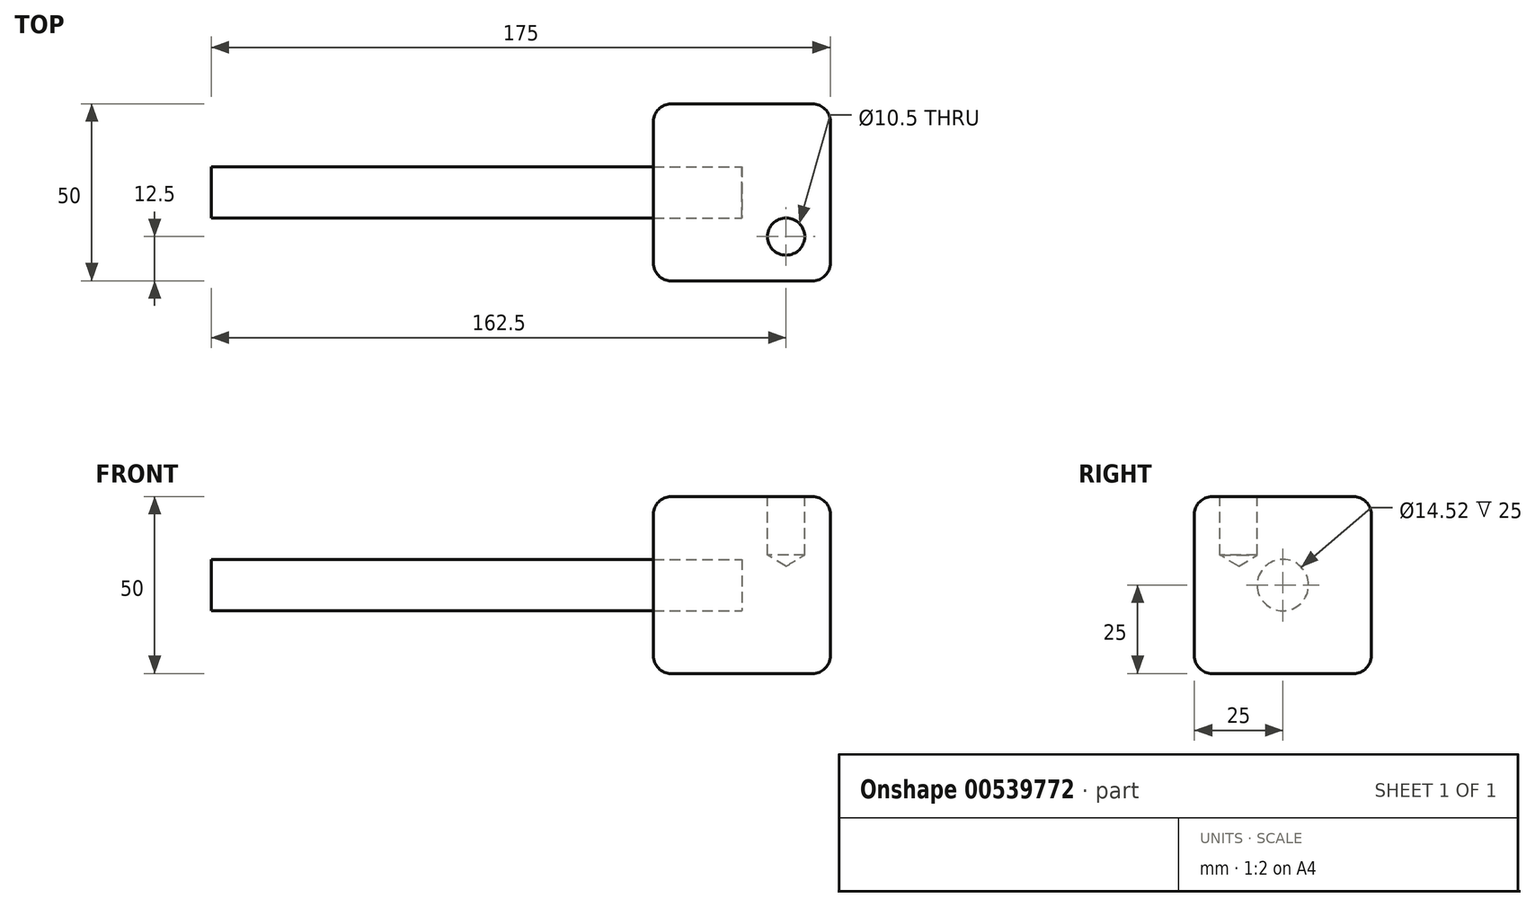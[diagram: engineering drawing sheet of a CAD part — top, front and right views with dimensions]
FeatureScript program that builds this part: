
annotation { "Feature Type Name" : "Feature", "Feature Type Description" : "" }
export const myFeature = defineFeature(function(context is Context, id is Id, definition is map)
    precondition{}
    {
        {
            var Q0;
            Q0=qCreatedBy(makeId("Front.planeOp"),FACE);
            var sketch = newSketch(context, id + "F0", { "sketchPlane" : qUnion([Q0])});
            skLineSegment(sketch, "E0.bottom", {"start": v(-25, 25) * mm, "end": v(25, 25) * mm});
            skLineSegment(sketch, "E0.top", {"start": v(-25, -25) * mm, "end": v(25, -25) * mm});
            skLineSegment(sketch, "E0.left", {"start": v(-25, 25) * mm, "end": v(-25, -25) * mm});
            skLineSegment(sketch, "E0.right", {"start": v(25, 25) * mm, "end": v(25, -25) * mm});
            skSolve(sketch);
        }
        {
            var Q0;
            Q0=makeQuery(id+"F0.imprint","IMPRINT",FACE,{"disambiguationData":[TD([[makeQuery(id+"F0.imprint","IMPRINT",EDGE,{"derivedFrom":sQuery(id+"F0.wireOp",EDGE,"E0.bottom")}),-1.0]])]});
            extrude(context, id + "F1", {"entities" : qUnion([Q0]), "endBound" : BoundingType.SYMMETRIC, "depth" : 50 * mm, "offsetDistance" : 25 * mm});
        }
        {
            var Q0;
            Q0=makeQuery(id+"F1.opExtrude","CAP_EDGE",EDGE,{"disambiguationData":[OSD([sQuery(id+"F0.wireOp",EDGE,"E0.left")])],"isStart":false});
            var Q1;
            Q1=makeQuery(id+"F1.opExtrude","SWEPT_EDGE",EDGE,{"disambiguationData":[OSD([sQuery(id+"F0.wireOp",EDGE,"E0.bottom"),sQuery(id+"F0.wireOp",EDGE,"E0.left")])]});
            var Q2;
            Q2=makeQuery(id+"F1.opExtrude","SWEPT_EDGE",EDGE,{"disambiguationData":[OSD([sQuery(id+"F0.wireOp",EDGE,"E0.bottom"),sQuery(id+"F0.wireOp",EDGE,"E0.right")])]});
            var Q3;
            Q3=makeQuery(id+"F1.opExtrude","CAP_EDGE",EDGE,{"disambiguationData":[OSD([sQuery(id+"F0.wireOp",EDGE,"E0.bottom")])],"isStart":true});
            var Q4;
            Q4=makeQuery(id+"F1.opExtrude","CAP_EDGE",EDGE,{"disambiguationData":[OSD([sQuery(id+"F0.wireOp",EDGE,"E0.bottom")])],"isStart":false});
            var Q5;
            Q5=makeQuery(id+"F1.opExtrude","CAP_EDGE",EDGE,{"disambiguationData":[OSD([sQuery(id+"F0.wireOp",EDGE,"E0.right")])],"isStart":false});
            var Q6;
            Q6=makeQuery(id+"F1.opExtrude","SWEPT_EDGE",EDGE,{"disambiguationData":[OSD([sQuery(id+"F0.wireOp",EDGE,"E0.top"),sQuery(id+"F0.wireOp",EDGE,"E0.right")])]});
            var Q7;
            Q7=makeQuery(id+"F1.opExtrude","CAP_EDGE",EDGE,{"disambiguationData":[OSD([sQuery(id+"F0.wireOp",EDGE,"E0.top")])],"isStart":false});
            var Q8;
            Q8=makeQuery(id+"F1.opExtrude","CAP_EDGE",EDGE,{"disambiguationData":[OSD([sQuery(id+"F0.wireOp",EDGE,"E0.right")])],"isStart":true});
            var Q9;
            Q9=makeQuery(id+"F1.opExtrude","CAP_EDGE",EDGE,{"disambiguationData":[OSD([sQuery(id+"F0.wireOp",EDGE,"E0.top")])],"isStart":true});
            var Q10;
            Q10=makeQuery(id+"F1.opExtrude","CAP_EDGE",EDGE,{"disambiguationData":[OSD([sQuery(id+"F0.wireOp",EDGE,"E0.left")])],"isStart":true});
            var Q11;
            Q11=makeQuery(id+"F1.opExtrude","SWEPT_FACE",FACE,{"disambiguationData":[OSD([sQuery(id+"F0.wireOp",EDGE,"E0.top")])]});
            fillet(context, id + "F2", {"entities" : qUnion([Q0, Q1, Q2, Q3, Q4, Q5, Q6, Q7, Q8, Q9, Q10, Q11]), "radius" : 5 * mm, "tangentPropagation" : true, "allowEdgeOverflow" : false});
        }
        {
            var Q0;
            Q0=makeQuery(id+"F1.opExtrude","SWEPT_FACE",FACE,{"disambiguationData":[OSD([sQuery(id+"F0.wireOp",EDGE,"E0.bottom")])]});
            var sketch = newSketch(context, id + "F3", { "sketchPlane" : qUnion([Q0])});
            skPoint(sketch, "E1", {"position": v(12.5, -12.5) * mm});
            skSolve(sketch);
        }
        {
            var Q0;
            Q0=sQuery(id+"F3.wireOp",VERTEX,"E1");
            var Q1;
            Q1=makeQuery(id+"F1.opExtrude","SWEPT_BODY",BODY,{"disambiguationData":[OSD([sQuery(id+"F0.wireOp",EDGE,"E0.bottom"),sQuery(id+"F0.wireOp",EDGE,"E0.top"),sQuery(id+"F0.wireOp",EDGE,"E0.left"),sQuery(id+"F0.wireOp",EDGE,"E0.right")])]});
            hole(context, id + "F4", {"style" : HoleStyle.SIMPLE, "endStyle" : HoleEndStyle.BLIND, "standardTappedOrClearance" : lookupTablePath({ "standard" : "ISO", "engagement" : "75%", "pitch" : "1.5 mm", "size" : "M12", "type" : "Tapped" }), "standardBlindInLast" : lookupTablePath({ "standard" : "ISO", "engagement" : "75%", "pitch" : "1.5 mm", "size" : "M12", "type" : "Tapped" }), "holeDiameter" : 10.5 * mm, "showTappedDepth" : true, "holeDepth" : 16.5 * mm, "isTappedThrough" : true, "tappedDepth" : 12 * mm, "tapClearance" : 3, "locations" : qUnion([Q0]), "scope" : qUnion([Q1]), "majorDiameter" : 12 * mm});
        }
        {
            var Q0;
            Q0=makeQuery(id+"F1.opExtrude","SWEPT_FACE",FACE,{"disambiguationData":[OSD([sQuery(id+"F0.wireOp",EDGE,"E0.left")])]});
            var sketch = newSketch(context, id + "F5", { "sketchPlane" : qUnion([Q0])});
            skCircle(sketch, "E2", {"center": v(0, 0) * mm, "radius": 7.26 * mm});
            skSolve(sketch);
        }
        {
            var Q0;
            Q0=makeQuery(id+"F5.imprint","IMPRINT",FACE,{"disambiguationData":[TD([[makeQuery(id+"F5.imprint","IMPRINT",EDGE,{"derivedFrom":sQuery(id+"F5.wireOp",EDGE,"E2")}),1.0]])]});
            extrude(context, id + "F6", {"entities" : qUnion([Q0]), "operationType" : NewBodyOperationType.REMOVE, "oppositeDirection" : true, "depth" : 25 * mm, "offsetDistance" : 25 * mm});
        }
        {
            var Q0;
            Q0=makeQuery(id+"F6.boolean.opBoolean","COPY",FACE,{"derivedFrom":makeQuery(id+"F6.opExtrude","CAP_FACE",FACE,{"disambiguationData":[OSD([sQuery(id+"F5.wireOp",EDGE,"E2")])],"isStart":false})});
            extrude(context, id + "F7", {"entities" : qUnion([Q0]), "depth" : 150 * mm, "offsetDistance" : 25 * mm});
        }
    });
